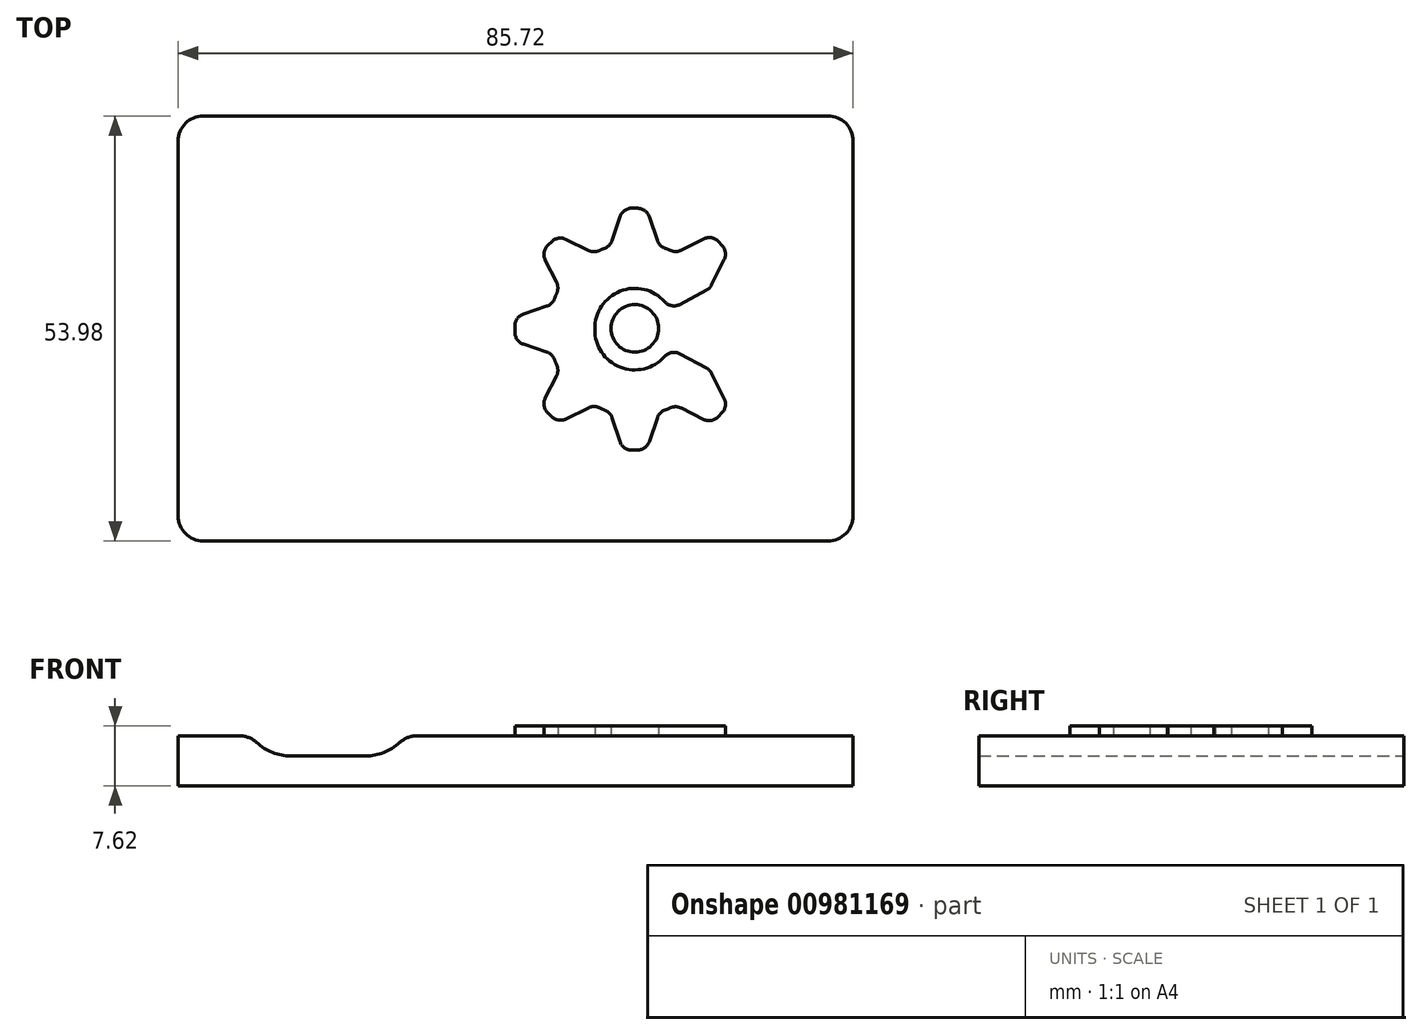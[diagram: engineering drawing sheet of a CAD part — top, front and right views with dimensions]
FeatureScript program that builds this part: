
annotation { "Feature Type Name" : "Feature", "Feature Type Description" : "" }
export const myFeature = defineFeature(function(context is Context, id is Id, definition is map)
    precondition{}
    {
        {
            var Q0;
            Q0=qCreatedBy(makeId("Top.planeOp"),FACE);
            var sketch = newSketch(context, id + "F0", { "sketchPlane" : qUnion([Q0])});
            skLineSegment(sketch, "E0.bottom", {"start": v(39.69, -26.99) * mm, "end": v(-39.69, -26.99) * mm});
            skLineSegment(sketch, "E0.top", {"start": v(39.69, 26.99) * mm, "end": v(-39.69, 26.99) * mm});
            skLineSegment(sketch, "E0.left", {"start": v(42.86, -23.81) * mm, "end": v(42.86, 23.81) * mm});
            skLineSegment(sketch, "E0.right", {"start": v(-42.86, -23.81) * mm, "end": v(-42.86, 23.81) * mm});
            skPoint(sketch, "E0.middle", {"position": v(0, 0) * mm});
            skPoint(sketch, "E1.visualSharp", {"position": v(-42.86, 26.99) * mm});
            skArc(sketch, "E1.filletArc", {"start": v(-39.69, 26.99) * mm, "mid": v(-41.93, 26.06) * mm, "end": v(-42.86, 23.81) * mm});
            skPoint(sketch, "E2.visualSharp", {"position": v(42.86, 26.99) * mm});
            skArc(sketch, "E2.filletArc", {"start": v(42.86, 23.81) * mm, "mid": v(41.93, 26.06) * mm, "end": v(39.69, 26.99) * mm});
            skPoint(sketch, "E3.visualSharp", {"position": v(42.86, -26.99) * mm});
            skArc(sketch, "E3.filletArc", {"start": v(39.69, -26.99) * mm, "mid": v(41.93, -26.06) * mm, "end": v(42.86, -23.81) * mm});
            skPoint(sketch, "E4.visualSharp", {"position": v(-42.86, -26.99) * mm});
            skArc(sketch, "E4.filletArc", {"start": v(-42.86, -23.81) * mm, "mid": v(-41.93, -26.06) * mm, "end": v(-39.69, -26.99) * mm});
            skSolve(sketch);
        }
        {
            var Q0;
            Q0=makeQuery(id+"F0.imprint","IMPRINT",FACE,{"disambiguationData":[TD([[makeQuery(id+"F0.imprint","IMPRINT",EDGE,{"derivedFrom":sQuery(id+"F0.wireOp",EDGE,"E0.bottom")}),-1.0]])]});
            extrude(context, id + "F1", {"entities" : qUnion([Q0]), "depth" : 6.35 * mm, "offsetDistance" : 25.4 * mm});
        }
        {
            var Q0;
            Q0=makeQuery(id+"F1.opExtrude","SWEPT_FACE",FACE,{"disambiguationData":[OSD([sQuery(id+"F0.wireOp",EDGE,"E0.top")])]});
            var sketch = newSketch(context, id + "F2", { "sketchPlane" : qUnion([Q0])});
            skLineSegment(sketch, "E5", {"start": v(19.05, 10.16) * mm, "end": v(28.57, 10.16) * mm});
            skArc(sketch, "E6.0.startCap", {"start": v(19.05, 3.81) * mm, "mid": v(12.7, 10.16) * mm, "end": v(19.05, 16.51) * mm});
            skArc(sketch, "E6.0.endCap", {"start": v(28.57, 16.51) * mm, "mid": v(34.92, 10.16) * mm, "end": v(28.57, 3.81) * mm});
            skLineSegment(sketch, "E6.0.left", {"start": v(19.05, 16.51) * mm, "end": v(28.57, 16.51) * mm});
            skLineSegment(sketch, "E6.0.right", {"start": v(19.05, 3.81) * mm, "end": v(28.57, 3.81) * mm});
            skSolve(sketch);
        }
        {
            var Q0;
            Q0 = qSketchRegion(id + "F2", true);
            extrude(context, id + "F3", {"entities" : qUnion([Q0]), "operationType" : NewBodyOperationType.REMOVE, "oppositeDirection" : true, "depth" : 76.2 * mm, "offsetDistance" : 25.4 * mm});
        }
        {
            var Q0;
            Q0=makeQuery(id+"F3.boolean.opBoolean","INTERSECT",EDGE,{"derivedFrom":[makeQuery(id+"F1.opExtrude","CAP_FACE",FACE,{"disambiguationData":[OSD([sQuery(id+"F0.wireOp",EDGE,"E0.bottom"),sQuery(id+"F0.wireOp",EDGE,"E0.top"),sQuery(id+"F0.wireOp",EDGE,"E0.left"),sQuery(id+"F0.wireOp",EDGE,"E0.right"),sQuery(id+"F0.wireOp",EDGE,"E1.filletArc"),sQuery(id+"F0.wireOp",EDGE,"E2.filletArc"),sQuery(id+"F0.wireOp",EDGE,"E3.filletArc"),sQuery(id+"F0.wireOp",EDGE,"E4.filletArc")])],"isStart":false}),makeQuery(id+"F3.opExtrude","SWEPT_FACE",FACE,{"disambiguationData":[OSD([sQuery(id+"F2.wireOp",EDGE,"E6.0.startCap")])]})]});
            var Q1;
            Q1=makeQuery(id+"F3.boolean.opBoolean","INTERSECT",EDGE,{"derivedFrom":[makeQuery(id+"F1.opExtrude","CAP_FACE",FACE,{"disambiguationData":[OSD([sQuery(id+"F0.wireOp",EDGE,"E0.bottom"),sQuery(id+"F0.wireOp",EDGE,"E0.top"),sQuery(id+"F0.wireOp",EDGE,"E0.left"),sQuery(id+"F0.wireOp",EDGE,"E0.right"),sQuery(id+"F0.wireOp",EDGE,"E1.filletArc"),sQuery(id+"F0.wireOp",EDGE,"E2.filletArc"),sQuery(id+"F0.wireOp",EDGE,"E3.filletArc"),sQuery(id+"F0.wireOp",EDGE,"E4.filletArc")])],"isStart":false}),makeQuery(id+"F3.opExtrude","SWEPT_FACE",FACE,{"disambiguationData":[OSD([sQuery(id+"F2.wireOp",EDGE,"E6.0.endCap")])]})]});
            fillet(context, id + "F4", {"entities" : qUnion([Q0, Q1]), "radius" : 3.17 * mm, "tangentPropagation" : true, "allowEdgeOverflow" : false});
        }
        {
            var Q0;
            {var subQ0=sQuery(id+"F0.wireOp",EDGE,"E2.filletArc");var subQ1=sQuery(id+"F0.wireOp",EDGE,"E0.left");var subQ2=sQuery(id+"F0.wireOp",EDGE,"E0.top");var subQ3=sQuery(id+"F0.wireOp",EDGE,"E0.bottom");var subQ4=sQuery(id+"F0.wireOp",EDGE,"E3.filletArc");Q0=makeQuery(id+"F3.boolean.opBoolean","SPLIT",FACE,{"disambiguationData":[TD([makeQuery(id+"F1.opExtrude","SWEPT_FACE",FACE,{"disambiguationData":[OSD([subQ1])]})])],"derivedFrom":makeQuery(id+"F1.opExtrude","CAP_FACE",FACE,{"disambiguationData":[OSD([subQ3,subQ2,subQ1,sQuery(id+"F0.wireOp",EDGE,"E0.right"),sQuery(id+"F0.wireOp",EDGE,"E1.filletArc"),subQ0,subQ4,sQuery(id+"F0.wireOp",EDGE,"E4.filletArc")])],"isStart":false})});}
            var sketch = newSketch(context, id + "F5", { "sketchPlane" : qUnion([Q0])});
            skLineSegment(sketch, "E7", {"start": v(-12.57, 0) * mm, "end": v(42.86, 0) * mm, "construction": true});
            skPoint(sketch, "E8.0", {"position": v(25.95, -10.99) * mm});
            skLineSegment(sketch, "E9.0", {"start": v(24.68, -5.26) * mm, "end": v(26.98, -9.89) * mm});
            skLineSegment(sketch, "E10.0", {"start": v(26.98, -9.89) * mm, "end": v(24.92, -12.09) * mm});
            skLineSegment(sketch, "E11.0", {"start": v(24.92, -12.09) * mm, "end": v(20.25, -9.71) * mm});
            skPoint(sketch, "E12.0", {"position": v(19.31, -10.24) * mm});
            skArc(sketch, "E13.0", {"start": v(20.25, -9.71) * mm, "mid": v(19.31, -10.24) * mm, "end": v(18.28, -10.5) * mm});
            skLineSegment(sketch, "E14.0", {"start": v(18.28, -10.5) * mm, "end": v(16.63, -15.4) * mm});
            skLineSegment(sketch, "E15.0", {"start": v(16.63, -15.4) * mm, "end": v(13.62, -15.5) * mm});
            skLineSegment(sketch, "E16.0", {"start": v(13.62, -15.5) * mm, "end": v(12, -10.52) * mm});
            skLineSegment(sketch, "E17.0", {"start": v(19.64, -2.56) * mm, "end": v(24.68, -5.26) * mm});
            skArc(sketch, "E18.0", {"start": v(10.05, -0.08) * mm, "mid": v(13.87, -5.1) * mm, "end": v(19.64, -2.56) * mm});
            skArc(sketch, "E19.0", {"start": v(19.64, 2.39) * mm, "mid": v(13.87, 4.93) * mm, "end": v(10.05, -0.08) * mm});
            skLineSegment(sketch, "E20.0", {"start": v(24.68, 5.1) * mm, "end": v(19.64, 2.39) * mm});
            skLineSegment(sketch, "E21.0", {"start": v(26.98, 9.72) * mm, "end": v(24.68, 5.1) * mm});
            skLineSegment(sketch, "E22.0", {"start": v(24.92, 11.92) * mm, "end": v(26.98, 9.72) * mm});
            skLineSegment(sketch, "E23.0", {"start": v(20.25, 9.55) * mm, "end": v(24.92, 11.92) * mm});
            skArc(sketch, "E24.0", {"start": v(18.28, 10.33) * mm, "mid": v(19.31, 10.07) * mm, "end": v(20.25, 9.55) * mm});
            skLineSegment(sketch, "E25.0", {"start": v(16.63, 15.23) * mm, "end": v(18.28, 10.33) * mm});
            skLineSegment(sketch, "E26.0", {"start": v(13.62, 15.33) * mm, "end": v(16.63, 15.23) * mm});
            skLineSegment(sketch, "E27.0", {"start": v(12, 10.35) * mm, "end": v(13.62, 15.33) * mm});
            skArc(sketch, "E28.0", {"start": v(10.04, 9.51) * mm, "mid": v(10.96, 10.06) * mm, "end": v(12, 10.35) * mm});
            skLineSegment(sketch, "E29.0", {"start": v(5.42, 11.82) * mm, "end": v(10.04, 9.51) * mm});
            skLineSegment(sketch, "E30.0", {"start": v(3.22, 9.75) * mm, "end": v(5.42, 11.82) * mm});
            skLineSegment(sketch, "E31.0", {"start": v(5.6, 5.08) * mm, "end": v(3.22, 9.75) * mm});
            skArc(sketch, "E32.0", {"start": v(4.8, 3.1) * mm, "mid": v(5.07, 4.15) * mm, "end": v(5.6, 5.08) * mm});
            skLineSegment(sketch, "E33.0", {"start": v(-0.1, 1.46) * mm, "end": v(4.8, 3.1) * mm});
            skLineSegment(sketch, "E34.0", {"start": v(-0.1, -1.63) * mm, "end": v(-0.1, 1.46) * mm});
            skLineSegment(sketch, "E35.0", {"start": v(4.8, -3.28) * mm, "end": v(-0.1, -1.63) * mm});
            skArc(sketch, "E36.0", {"start": v(5.6, -5.25) * mm, "mid": v(5.07, -4.31) * mm, "end": v(4.8, -3.28) * mm});
            skLineSegment(sketch, "E37.0", {"start": v(3.22, -9.92) * mm, "end": v(5.6, -5.25) * mm});
            skLineSegment(sketch, "E38.0", {"start": v(5.42, -11.98) * mm, "end": v(3.22, -9.92) * mm});
            skLineSegment(sketch, "E39.0", {"start": v(10.04, -9.68) * mm, "end": v(5.42, -11.98) * mm});
            skArc(sketch, "E40.0", {"start": v(12, -10.52) * mm, "mid": v(10.96, -10.23) * mm, "end": v(10.04, -9.68) * mm});
            skCircle(sketch, "E41", {"center": v(15.14, 0) * mm, "radius": 3.02 * mm});
            skSolve(sketch);
        }
        {
            var Q0;
            Q0 = qSketchRegion(id + "F5", true);
            extrude(context, id + "F6", {"entities" : qUnion([Q0]), "depth" : 1.27 * mm, "offsetDistance" : 25.4 * mm});
        }
        {
            var Q0;
            Q0=makeQuery(id+"F6.opExtrude","SWEPT_EDGE",EDGE,{"disambiguationData":[OSD([sQuery(id+"F5.wireOp",EDGE,"E37.0"),sQuery(id+"F5.wireOp",EDGE,"E38.0")])]});
            var Q1;
            Q1=makeQuery(id+"F6.opExtrude","SWEPT_EDGE",EDGE,{"disambiguationData":[OSD([sQuery(id+"F5.wireOp",EDGE,"E38.0"),sQuery(id+"F5.wireOp",EDGE,"E39.0")])]});
            var Q2;
            Q2=makeQuery(id+"F6.opExtrude","SWEPT_EDGE",EDGE,{"disambiguationData":[OSD([sQuery(id+"F5.wireOp",EDGE,"E39.0"),sQuery(id+"F5.wireOp",EDGE,"E40.0")])]});
            var Q3;
            Q3=makeQuery(id+"F6.opExtrude","SWEPT_EDGE",EDGE,{"disambiguationData":[OSD([sQuery(id+"F5.wireOp",EDGE,"E16.0"),sQuery(id+"F5.wireOp",EDGE,"E40.0")])]});
            var Q4;
            Q4=makeQuery(id+"F6.opExtrude","SWEPT_EDGE",EDGE,{"disambiguationData":[OSD([sQuery(id+"F5.wireOp",EDGE,"E15.0"),sQuery(id+"F5.wireOp",EDGE,"E16.0")])]});
            var Q5;
            Q5=makeQuery(id+"F6.opExtrude","SWEPT_EDGE",EDGE,{"disambiguationData":[OSD([sQuery(id+"F5.wireOp",EDGE,"E14.0"),sQuery(id+"F5.wireOp",EDGE,"E15.0")])]});
            var Q6;
            Q6=makeQuery(id+"F6.opExtrude","SWEPT_EDGE",EDGE,{"disambiguationData":[OSD([sQuery(id+"F5.wireOp",EDGE,"E10.0"),sQuery(id+"F5.wireOp",EDGE,"E11.0")])]});
            var Q7;
            Q7=makeQuery(id+"F6.opExtrude","SWEPT_EDGE",EDGE,{"disambiguationData":[OSD([sQuery(id+"F5.wireOp",EDGE,"E11.0"),sQuery(id+"F5.wireOp",EDGE,"E13.0")])]});
            var Q8;
            Q8=makeQuery(id+"F6.opExtrude","SWEPT_EDGE",EDGE,{"disambiguationData":[OSD([sQuery(id+"F5.wireOp",EDGE,"E13.0"),sQuery(id+"F5.wireOp",EDGE,"E14.0")])]});
            var Q9;
            Q9=makeQuery(id+"F6.opExtrude","SWEPT_EDGE",EDGE,{"disambiguationData":[OSD([sQuery(id+"F5.wireOp",EDGE,"E9.0"),sQuery(id+"F5.wireOp",EDGE,"E10.0")])]});
            var Q10;
            Q10=makeQuery(id+"F6.opExtrude","SWEPT_EDGE",EDGE,{"disambiguationData":[OSD([sQuery(id+"F5.wireOp",EDGE,"E9.0"),sQuery(id+"F5.wireOp",EDGE,"E17.0")])]});
            var Q11;
            Q11=makeQuery(id+"F6.opExtrude","SWEPT_EDGE",EDGE,{"disambiguationData":[OSD([sQuery(id+"F5.wireOp",EDGE,"E17.0"),sQuery(id+"F5.wireOp",EDGE,"E18.0")])]});
            var Q12;
            Q12=makeQuery(id+"F6.opExtrude","SWEPT_EDGE",EDGE,{"disambiguationData":[OSD([sQuery(id+"F5.wireOp",EDGE,"E19.0"),sQuery(id+"F5.wireOp",EDGE,"E20.0")])]});
            var Q13;
            Q13=makeQuery(id+"F6.opExtrude","SWEPT_EDGE",EDGE,{"disambiguationData":[OSD([sQuery(id+"F5.wireOp",EDGE,"E20.0"),sQuery(id+"F5.wireOp",EDGE,"E21.0")])]});
            var Q14;
            Q14=makeQuery(id+"F6.opExtrude","SWEPT_EDGE",EDGE,{"disambiguationData":[OSD([sQuery(id+"F5.wireOp",EDGE,"E21.0"),sQuery(id+"F5.wireOp",EDGE,"E22.0")])]});
            var Q15;
            Q15=makeQuery(id+"F6.opExtrude","SWEPT_EDGE",EDGE,{"disambiguationData":[OSD([sQuery(id+"F5.wireOp",EDGE,"E22.0"),sQuery(id+"F5.wireOp",EDGE,"E23.0")])]});
            var Q16;
            Q16=makeQuery(id+"F6.opExtrude","SWEPT_EDGE",EDGE,{"disambiguationData":[OSD([sQuery(id+"F5.wireOp",EDGE,"E23.0"),sQuery(id+"F5.wireOp",EDGE,"E24.0")])]});
            var Q17;
            Q17=makeQuery(id+"F6.opExtrude","SWEPT_EDGE",EDGE,{"disambiguationData":[OSD([sQuery(id+"F5.wireOp",EDGE,"E24.0"),sQuery(id+"F5.wireOp",EDGE,"E25.0")])]});
            var Q18;
            Q18=makeQuery(id+"F6.opExtrude","SWEPT_EDGE",EDGE,{"disambiguationData":[OSD([sQuery(id+"F5.wireOp",EDGE,"E25.0"),sQuery(id+"F5.wireOp",EDGE,"E26.0")])]});
            var Q19;
            Q19=makeQuery(id+"F6.opExtrude","SWEPT_EDGE",EDGE,{"disambiguationData":[OSD([sQuery(id+"F5.wireOp",EDGE,"E26.0"),sQuery(id+"F5.wireOp",EDGE,"E27.0")])]});
            var Q20;
            Q20=makeQuery(id+"F6.opExtrude","SWEPT_EDGE",EDGE,{"disambiguationData":[OSD([sQuery(id+"F5.wireOp",EDGE,"E27.0"),sQuery(id+"F5.wireOp",EDGE,"E28.0")])]});
            var Q21;
            Q21=makeQuery(id+"F6.opExtrude","SWEPT_EDGE",EDGE,{"disambiguationData":[OSD([sQuery(id+"F5.wireOp",EDGE,"E28.0"),sQuery(id+"F5.wireOp",EDGE,"E29.0")])]});
            var Q22;
            Q22=makeQuery(id+"F6.opExtrude","SWEPT_EDGE",EDGE,{"disambiguationData":[OSD([sQuery(id+"F5.wireOp",EDGE,"E29.0"),sQuery(id+"F5.wireOp",EDGE,"E30.0")])]});
            var Q23;
            Q23=makeQuery(id+"F6.opExtrude","SWEPT_EDGE",EDGE,{"disambiguationData":[OSD([sQuery(id+"F5.wireOp",EDGE,"E30.0"),sQuery(id+"F5.wireOp",EDGE,"E31.0")])]});
            var Q24;
            Q24=makeQuery(id+"F6.opExtrude","SWEPT_EDGE",EDGE,{"disambiguationData":[OSD([sQuery(id+"F5.wireOp",EDGE,"E32.0"),sQuery(id+"F5.wireOp",EDGE,"E33.0")])]});
            var Q25;
            Q25=makeQuery(id+"F6.opExtrude","SWEPT_EDGE",EDGE,{"disambiguationData":[OSD([sQuery(id+"F5.wireOp",EDGE,"E31.0"),sQuery(id+"F5.wireOp",EDGE,"E32.0")])]});
            var Q26;
            Q26=makeQuery(id+"F6.opExtrude","SWEPT_EDGE",EDGE,{"disambiguationData":[OSD([sQuery(id+"F5.wireOp",EDGE,"E36.0"),sQuery(id+"F5.wireOp",EDGE,"E37.0")])]});
            var Q27;
            Q27=makeQuery(id+"F6.opExtrude","SWEPT_EDGE",EDGE,{"disambiguationData":[OSD([sQuery(id+"F5.wireOp",EDGE,"E35.0"),sQuery(id+"F5.wireOp",EDGE,"E36.0")])]});
            var Q28;
            Q28=makeQuery(id+"F6.opExtrude","SWEPT_EDGE",EDGE,{"disambiguationData":[OSD([sQuery(id+"F5.wireOp",EDGE,"E34.0"),sQuery(id+"F5.wireOp",EDGE,"E35.0")])]});
            var Q29;
            Q29=makeQuery(id+"F6.opExtrude","SWEPT_EDGE",EDGE,{"disambiguationData":[OSD([sQuery(id+"F5.wireOp",EDGE,"E33.0"),sQuery(id+"F5.wireOp",EDGE,"E34.0")])]});
            fillet(context, id + "F7", {"entities" : qUnion([Q0, Q1, Q2, Q3, Q4, Q5, Q6, Q7, Q8, Q9, Q10, Q11, Q12, Q13, Q14, Q15, Q16, Q17, Q18, Q19, Q20, Q21, Q22, Q23, Q24, Q25, Q26, Q27, Q28, Q29]), "radius" : 1.6 * mm, "tangentPropagation" : true, "allowEdgeOverflow" : false});
        }
    });
